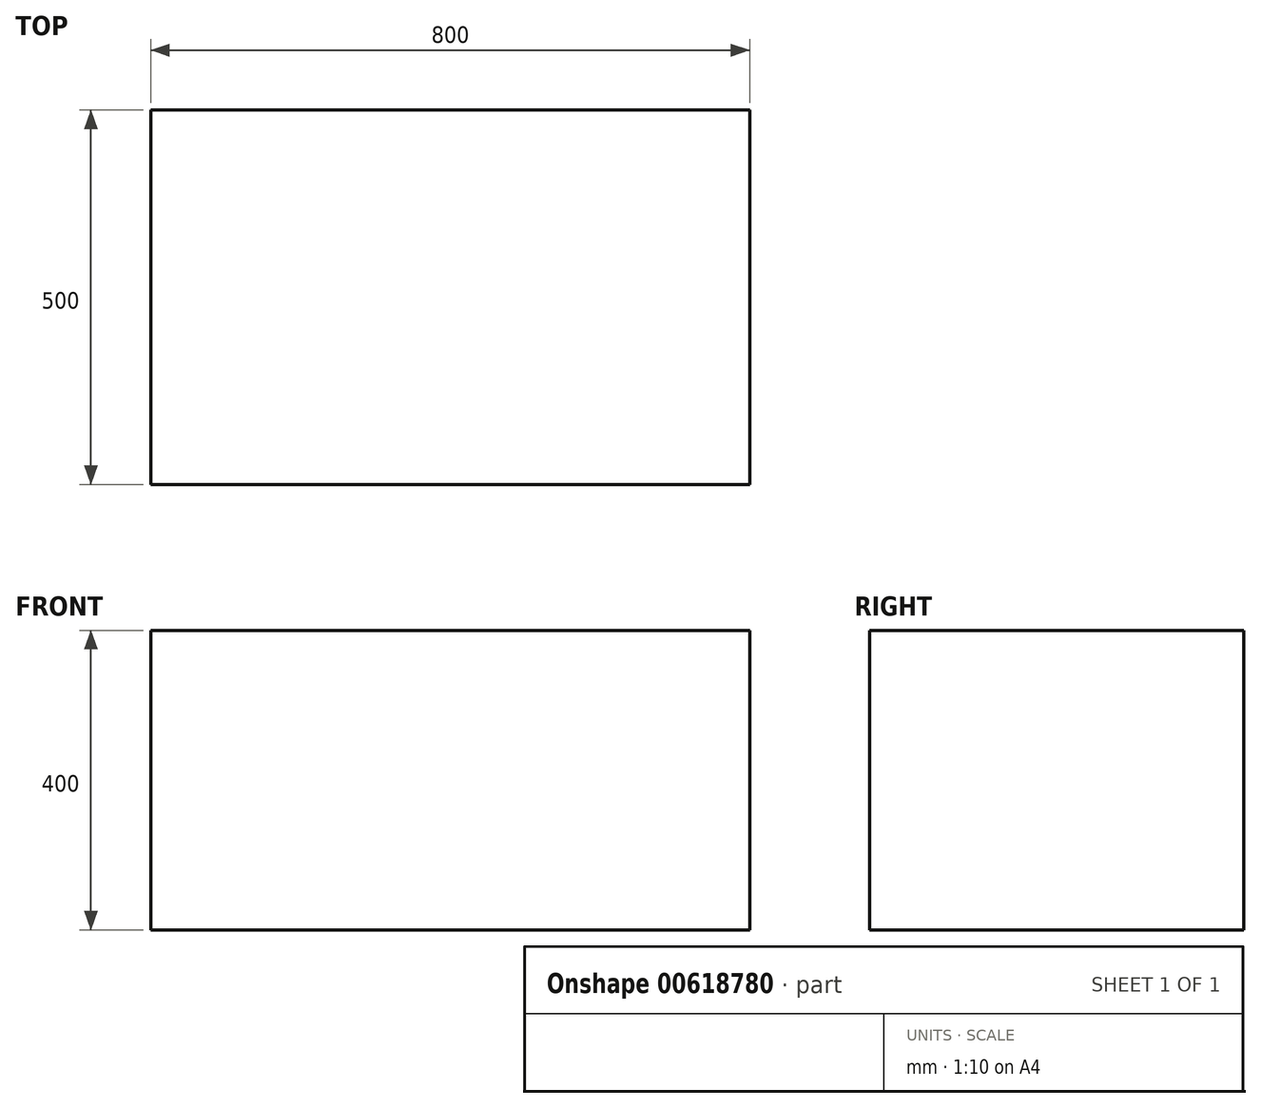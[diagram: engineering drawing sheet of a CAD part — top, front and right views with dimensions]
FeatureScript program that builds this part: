
annotation { "Feature Type Name" : "Feature", "Feature Type Description" : "" }
export const myFeature = defineFeature(function(context is Context, id is Id, definition is map)
    precondition{}
    {
        {
            var Q0;
            Q0=qCreatedBy(makeId("Top.planeOp"),FACE);
            var sketch = newSketch(context, id + "F0", { "sketchPlane" : qUnion([Q0])});
            skLineSegment(sketch, "E0.bottom", {"start": v(400, 250) * mm, "end": v(-400, 250) * mm});
            skLineSegment(sketch, "E0.top", {"start": v(400, -250) * mm, "end": v(-400, -250) * mm});
            skLineSegment(sketch, "E0.left", {"start": v(400, 250) * mm, "end": v(400, -250) * mm});
            skLineSegment(sketch, "E0.right", {"start": v(-400, 250) * mm, "end": v(-400, -250) * mm});
            skPoint(sketch, "E0.middle", {"position": v(0, 0) * mm});
            skSolve(sketch);
        }
        {
            var Q0;
            Q0=makeQuery(id+"F0.imprint","IMPRINT",FACE,{"disambiguationData":[TD([[makeQuery(id+"F0.imprint","IMPRINT",EDGE,{"derivedFrom":sQuery(id+"F0.wireOp",EDGE,"E0.bottom")}),1.0]])]});
            extrude(context, id + "F1", {"entities" : qUnion([Q0]), "oppositeDirection" : true, "depth" : 400 * mm, "offsetDistance" : 25 * mm});
        }
    });
